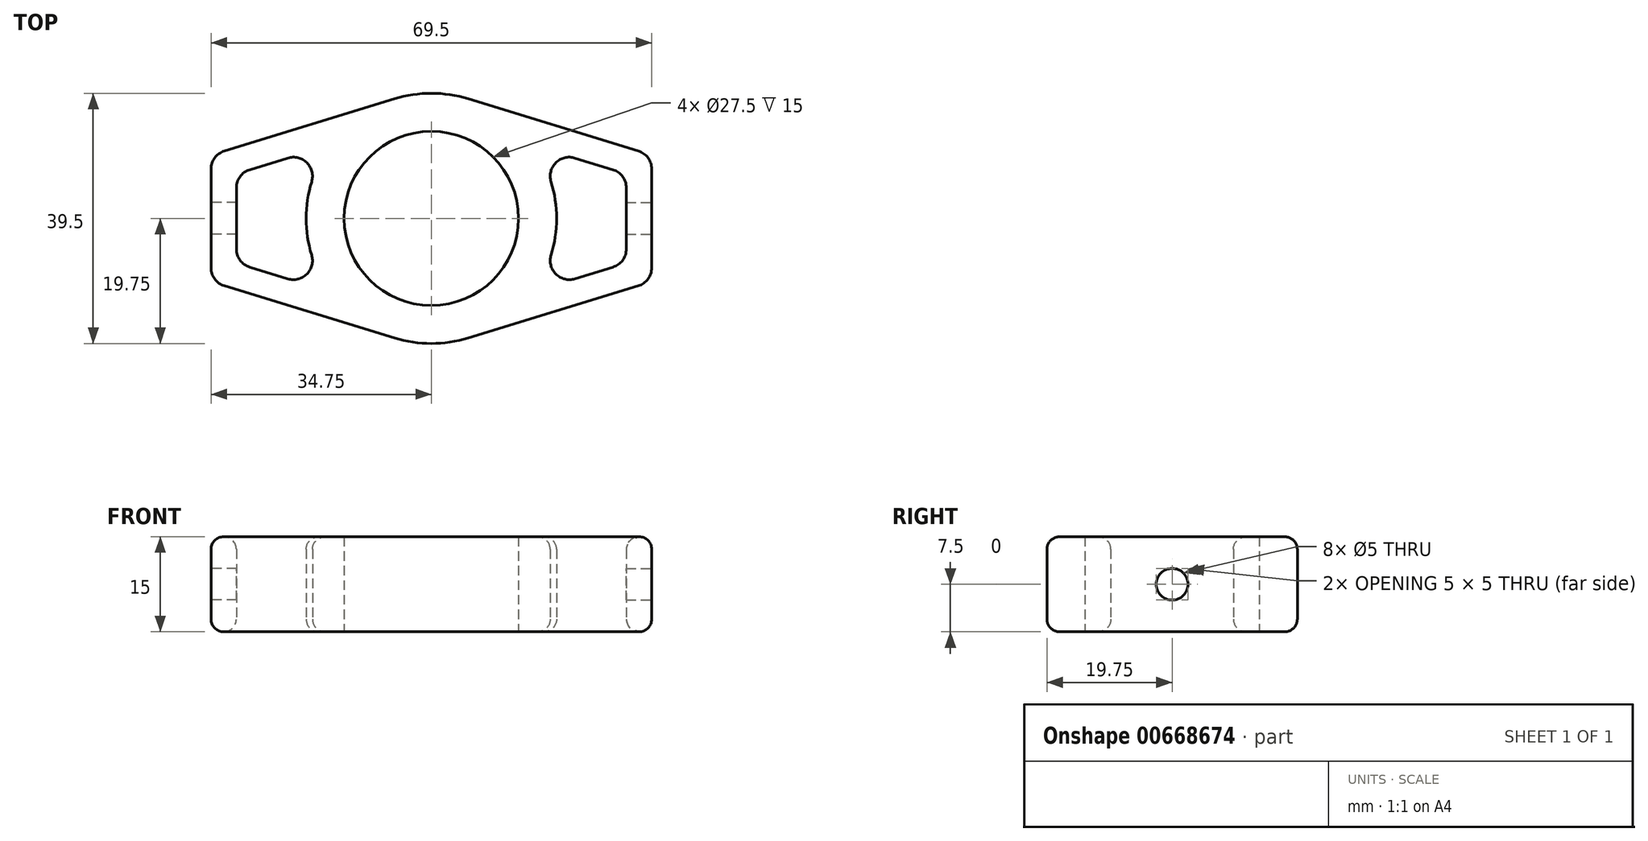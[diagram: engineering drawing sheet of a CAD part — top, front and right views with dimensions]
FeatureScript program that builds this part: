
annotation { "Feature Type Name" : "Feature", "Feature Type Description" : "" }
export const myFeature = defineFeature(function(context is Context, id is Id, definition is map)
    precondition{}
    {
        {
            var Q0;
            Q0=qCreatedBy(makeId("Top.planeOp"),FACE);
            var sketch = newSketch(context, id + "F0", { "sketchPlane" : qUnion([Q0])});
            skCircle(sketch, "E0", {"center": v(0, 0) * mm, "radius": 13.75 * mm});
            skArc(sketch, "E1", {"start": v(-16.01, 11.56) * mm, "mid": v(-19.75, 0) * mm, "end": v(-16.01, -11.56) * mm});
            skLineSegment(sketch, "E2", {"start": v(-34.75, -10) * mm, "end": v(-34.75, 10) * mm});
            skLineSegment(sketch, "E3", {"start": v(34.75, 10) * mm, "end": v(34.75, -10) * mm});
            skLineSegment(sketch, "E4", {"start": v(-34.75, -10) * mm, "end": v(-5.8, -18.88) * mm});
            skLineSegment(sketch, "E5", {"start": v(34.75, -10) * mm, "end": v(5.8, -18.88) * mm});
            skLineSegment(sketch, "E6", {"start": v(34.75, 10) * mm, "end": v(5.8, 18.88) * mm});
            skLineSegment(sketch, "E7", {"start": v(30.75, 7.04) * mm, "end": v(30.75, -7.04) * mm});
            skLineSegment(sketch, "E8", {"start": v(30.75, -7.04) * mm, "end": v(16.01, -11.56) * mm});
            skLineSegment(sketch, "E9", {"start": v(30.75, 7.04) * mm, "end": v(16.01, 11.56) * mm});
            skLineSegment(sketch, "E10", {"start": v(-34.75, 10) * mm, "end": v(-5.8, 18.88) * mm});
            skLineSegment(sketch, "E11", {"start": v(-30.75, 7.04) * mm, "end": v(-30.75, -7.04) * mm});
            skLineSegment(sketch, "E12", {"start": v(-30.75, -7.04) * mm, "end": v(-16.01, -11.56) * mm});
            skLineSegment(sketch, "E13", {"start": v(-30.75, 7.04) * mm, "end": v(-16.01, 11.56) * mm});
            skArc(sketch, "E14.trimOffspring", {"start": v(5.8, 18.88) * mm, "mid": v(0, 19.75) * mm, "end": v(-5.8, 18.88) * mm});
            skArc(sketch, "E15.trimOffspring", {"start": v(16.01, -11.56) * mm, "mid": v(19.75, 0) * mm, "end": v(16.01, 11.56) * mm});
            skArc(sketch, "E16.trimOffspring", {"start": v(-5.8, -18.88) * mm, "mid": v(0, -19.75) * mm, "end": v(5.8, -18.88) * mm});
            skSolve(sketch);
        }
        {
            var Q0;
            Q0 = qSketchRegion(id + "F0", true);
            extrude(context, id + "F1", {"entities" : qUnion([Q0]), "depth" : 15 * mm, "offsetDistance" : 25 * mm});
        }
        {
            var Q0;
            Q0=makeQuery(id+"F1.opExtrude","SWEPT_EDGE",EDGE,{"disambiguationData":[OSD([sQuery(id+"F0.wireOp",EDGE,"E11"),sQuery(id+"F0.wireOp",EDGE,"E13")])]});
            var Q1;
            Q1=makeQuery(id+"F1.opExtrude","SWEPT_EDGE",EDGE,{"disambiguationData":[OSD([sQuery(id+"F0.wireOp",EDGE,"E11"),sQuery(id+"F0.wireOp",EDGE,"E12")])]});
            var Q2;
            Q2=makeQuery(id+"F1.opExtrude","SWEPT_EDGE",EDGE,{"disambiguationData":[OSD([sQuery(id+"F0.wireOp",EDGE,"E1"),sQuery(id+"F0.wireOp",EDGE,"E13")])]});
            var Q3;
            Q3=makeQuery(id+"F1.opExtrude","SWEPT_EDGE",EDGE,{"disambiguationData":[OSD([sQuery(id+"F0.wireOp",EDGE,"E1"),sQuery(id+"F0.wireOp",EDGE,"E12")])]});
            fillet(context, id + "F2", {"entities" : qUnion([Q0, Q1, Q2, Q3]), "radius" : 3 * mm, "tangentPropagation" : true, "allowEdgeOverflow" : false});
        }
        {
            var Q0;
            Q0=makeQuery(id+"F1.opExtrude","SWEPT_EDGE",EDGE,{"disambiguationData":[OSD([sQuery(id+"F0.wireOp",EDGE,"E9"),sQuery(id+"F0.wireOp",EDGE,"E15.trimOffspring")])]});
            var Q1;
            Q1=makeQuery(id+"F1.opExtrude","SWEPT_EDGE",EDGE,{"disambiguationData":[OSD([sQuery(id+"F0.wireOp",EDGE,"E7"),sQuery(id+"F0.wireOp",EDGE,"E9")])]});
            var Q2;
            Q2=makeQuery(id+"F1.opExtrude","SWEPT_EDGE",EDGE,{"disambiguationData":[OSD([sQuery(id+"F0.wireOp",EDGE,"E7"),sQuery(id+"F0.wireOp",EDGE,"E8")])]});
            var Q3;
            Q3=makeQuery(id+"F1.opExtrude","SWEPT_EDGE",EDGE,{"disambiguationData":[OSD([sQuery(id+"F0.wireOp",EDGE,"E8"),sQuery(id+"F0.wireOp",EDGE,"E15.trimOffspring")])]});
            fillet(context, id + "F3", {"entities" : qUnion([Q0, Q1, Q2, Q3]), "radius" : 3 * mm, "tangentPropagation" : true, "allowEdgeOverflow" : false});
        }
        {
            var Q0;
            Q0=makeQuery(id+"F1.opExtrude","SWEPT_EDGE",EDGE,{"disambiguationData":[OSD([sQuery(id+"F0.wireOp",EDGE,"E3"),sQuery(id+"F0.wireOp",EDGE,"E5")])]});
            var Q1;
            Q1=makeQuery(id+"F1.opExtrude","SWEPT_EDGE",EDGE,{"disambiguationData":[OSD([sQuery(id+"F0.wireOp",EDGE,"E3"),sQuery(id+"F0.wireOp",EDGE,"E6")])]});
            fillet(context, id + "F4", {"entities" : qUnion([Q0, Q1]), "radius" : 3 * mm, "tangentPropagation" : true, "allowEdgeOverflow" : false});
        }
        {
            var Q0;
            Q0=makeQuery(id+"F1.opExtrude","SWEPT_EDGE",EDGE,{"disambiguationData":[OSD([sQuery(id+"F0.wireOp",EDGE,"E2"),sQuery(id+"F0.wireOp",EDGE,"E10")])]});
            var Q1;
            Q1=makeQuery(id+"F1.opExtrude","SWEPT_EDGE",EDGE,{"disambiguationData":[OSD([sQuery(id+"F0.wireOp",EDGE,"E2"),sQuery(id+"F0.wireOp",EDGE,"E4")])]});
            fillet(context, id + "F5", {"entities" : qUnion([Q0, Q1]), "radius" : 3 * mm, "tangentPropagation" : true, "allowEdgeOverflow" : false});
        }
        {
            var Q0;
            Q0=makeQuery(id+"F1.opExtrude","CAP_EDGE",EDGE,{"disambiguationData":[OSD([sQuery(id+"F0.wireOp",EDGE,"E10")])],"isStart":false});
            fillet(context, id + "F6", {"entities" : qUnion([Q0]), "radius" : 2 * mm, "tangentPropagation" : true, "allowEdgeOverflow" : false});
        }
        {
            var Q0;
            Q0=makeQuery(id+"F1.opExtrude","CAP_EDGE",EDGE,{"disambiguationData":[OSD([sQuery(id+"F0.wireOp",EDGE,"E4")])],"isStart":true});
            fillet(context, id + "F7", {"entities" : qUnion([Q0]), "radius" : 2 * mm, "tangentPropagation" : true, "allowEdgeOverflow" : false});
        }
        {
            var Q0;
            Q0=makeQuery(id+"F1.opExtrude","CAP_EDGE",EDGE,{"disambiguationData":[OSD([sQuery(id+"F0.wireOp",EDGE,"E13")])],"isStart":false});
            fillet(context, id + "F8", {"entities" : qUnion([Q0]), "radius" : 2 * mm, "tangentPropagation" : true, "allowEdgeOverflow" : false});
        }
        {
            var Q0;
            Q0=makeQuery(id+"F1.opExtrude","CAP_EDGE",EDGE,{"disambiguationData":[OSD([sQuery(id+"F0.wireOp",EDGE,"E9")])],"isStart":false});
            fillet(context, id + "F9", {"entities" : qUnion([Q0]), "radius" : 2 * mm, "tangentPropagation" : true, "allowEdgeOverflow" : false});
        }
        {
            var Q0;
            Q0=makeQuery(id+"F1.opExtrude","CAP_EDGE",EDGE,{"disambiguationData":[OSD([sQuery(id+"F0.wireOp",EDGE,"E12")])],"isStart":true});
            fillet(context, id + "F10", {"entities" : qUnion([Q0]), "radius" : 2 * mm, "tangentPropagation" : true, "allowEdgeOverflow" : false});
        }
        {
            var Q0;
            Q0=makeQuery(id+"F1.opExtrude","CAP_EDGE",EDGE,{"disambiguationData":[OSD([sQuery(id+"F0.wireOp",EDGE,"E8")])],"isStart":true});
            fillet(context, id + "F11", {"entities" : qUnion([Q0]), "radius" : 2 * mm, "tangentPropagation" : true, "allowEdgeOverflow" : false});
        }
        {
            var Q0;
            Q0=makeQuery(id+"F1.opExtrude","SWEPT_FACE",FACE,{"disambiguationData":[OSD([sQuery(id+"F0.wireOp",EDGE,"E2")])]});
            var sketch = newSketch(context, id + "F12", { "sketchPlane" : qUnion([Q0])});
            skCircle(sketch, "E17", {"center": v(0, 7.5) * mm, "radius": 2.5 * mm});
            skSolve(sketch);
        }
        {
            var Q0;
            Q0=makeQuery(id+"F12.imprint","IMPRINT",FACE,{"disambiguationData":[TD([[makeQuery(id+"F12.imprint","IMPRINT",EDGE,{"derivedFrom":sQuery(id+"F12.wireOp",EDGE,"E17")}),1.0]])]});
            extrude(context, id + "F13", {"entities" : qUnion([Q0]), "operationType" : NewBodyOperationType.REMOVE, "oppositeDirection" : true, "depth" : 5 * mm, "offsetDistance" : 25 * mm});
        }
        {
            var Q0;
            Q0=makeQuery(id+"F1.opExtrude","SWEPT_FACE",FACE,{"disambiguationData":[OSD([sQuery(id+"F0.wireOp",EDGE,"E3")])]});
            var sketch = newSketch(context, id + "F14", { "sketchPlane" : qUnion([Q0])});
            skCircle(sketch, "E18", {"center": v(0, 7.5) * mm, "radius": 2.5 * mm});
            skSolve(sketch);
        }
        {
            var Q0;
            Q0=makeQuery(id+"F14.imprint","IMPRINT",FACE,{"disambiguationData":[TD([[makeQuery(id+"F14.imprint","IMPRINT",EDGE,{"derivedFrom":sQuery(id+"F14.wireOp",EDGE,"E18")}),1.0]])]});
            extrude(context, id + "F15", {"entities" : qUnion([Q0]), "operationType" : NewBodyOperationType.REMOVE, "oppositeDirection" : true, "depth" : 5 * mm, "offsetDistance" : 25 * mm});
        }
    });
